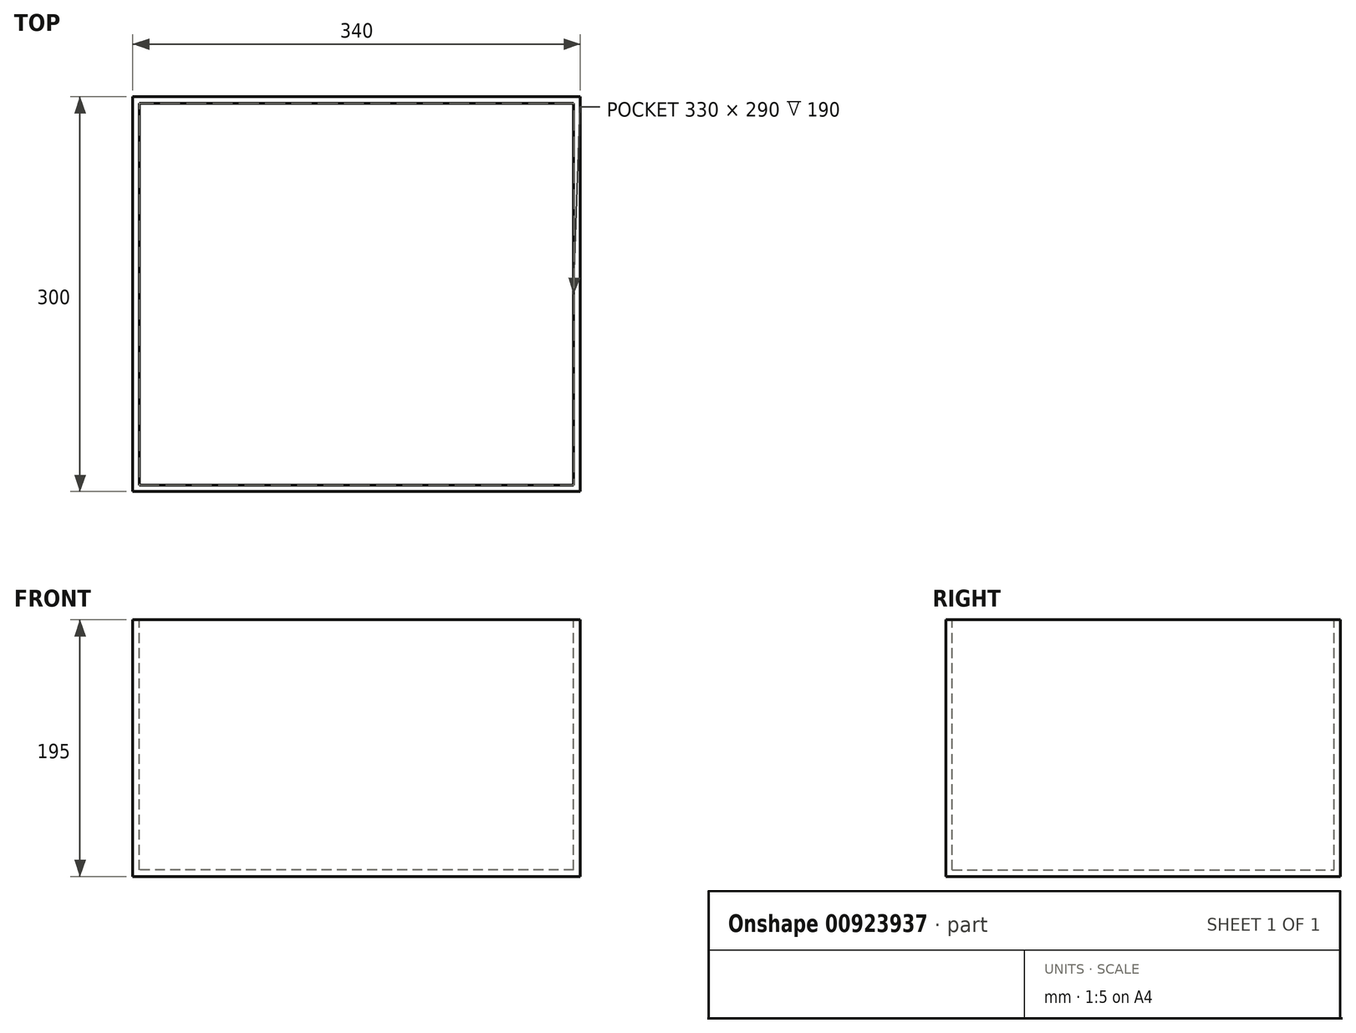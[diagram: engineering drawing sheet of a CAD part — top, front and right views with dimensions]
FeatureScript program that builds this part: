
annotation { "Feature Type Name" : "Feature", "Feature Type Description" : "" }
export const myFeature = defineFeature(function(context is Context, id is Id, definition is map)
    precondition{}
    {
        {
            var Q0;
            Q0=qCreatedBy(makeId("Top.planeOp"),FACE);
            var sketch = newSketch(context, id + "F0", { "sketchPlane" : qUnion([Q0])});
            skLineSegment(sketch, "E0.bottom", {"start": v(168.68, -145) * mm, "end": v(-161.32, -145) * mm});
            skLineSegment(sketch, "E0.top", {"start": v(168.68, 145) * mm, "end": v(-161.32, 145) * mm});
            skLineSegment(sketch, "E0.left", {"start": v(168.68, -145) * mm, "end": v(168.68, 145) * mm});
            skLineSegment(sketch, "E0.right", {"start": v(-161.32, -145) * mm, "end": v(-161.32, 145) * mm});
            skPoint(sketch, "E0.middle", {"position": v(3.68, 0) * mm});
            skLineSegment(sketch, "E1.bottom", {"start": v(173.68, -150) * mm, "end": v(-166.32, -150) * mm});
            skLineSegment(sketch, "E1.top", {"start": v(173.68, 150) * mm, "end": v(-166.32, 150) * mm});
            skLineSegment(sketch, "E1.left", {"start": v(173.68, -150) * mm, "end": v(173.68, 150) * mm});
            skLineSegment(sketch, "E1.right", {"start": v(-166.32, -150) * mm, "end": v(-166.32, 150) * mm});
            skSolve(sketch);
        }
        {
            var Q0;
            Q0 = qSketchRegion(id + "F0", true);
            var Q1;
            Q1=makeQuery(id+"F0.imprint","IMPRINT",FACE,{"disambiguationData":[TD([[makeQuery(id+"F0.imprint","IMPRINT",EDGE,{"derivedFrom":sQuery(id+"F0.wireOp",EDGE,"E0.bottom")}),-1.0]])]});
            extrude(context, id + "F1", {"entities" : qUnion([Q0, Q1]), "depth" : 195 * mm, "offsetDistance" : 25 * mm});
        }
        {
            var Q0;
            Q0=makeQuery(id+"F1.opExtrude","CAP_FACE",FACE,{"disambiguationData":[OSD([sQuery(id+"F0.wireOp",EDGE,"E1.bottom"),sQuery(id+"F0.wireOp",EDGE,"E1.top"),sQuery(id+"F0.wireOp",EDGE,"E1.left"),sQuery(id+"F0.wireOp",EDGE,"E1.right")])],"isStart":false});
            var sketch = newSketch(context, id + "F2", { "sketchPlane" : qUnion([Q0])});
            skLineSegment(sketch, "E2.bottom", {"start": v(168.68, -145) * mm, "end": v(-161.32, -145) * mm});
            skLineSegment(sketch, "E2.top", {"start": v(168.68, 145) * mm, "end": v(-161.32, 145) * mm});
            skLineSegment(sketch, "E2.left", {"start": v(168.68, -145) * mm, "end": v(168.68, 145) * mm});
            skLineSegment(sketch, "E2.right", {"start": v(-161.32, -145) * mm, "end": v(-161.32, 145) * mm});
            skPoint(sketch, "E2.middle", {"position": v(-68.35, 30.33) * mm});
            skLineSegment(sketch, "E3.bottom", {"start": v(173.68, -150) * mm, "end": v(-166.32, -150) * mm});
            skLineSegment(sketch, "E3.top", {"start": v(173.68, 150) * mm, "end": v(-166.32, 150) * mm});
            skLineSegment(sketch, "E3.left", {"start": v(173.68, -150) * mm, "end": v(173.68, 150) * mm});
            skLineSegment(sketch, "E3.right", {"start": v(-166.32, -150) * mm, "end": v(-166.32, 150) * mm});
            skPoint(sketch, "E3.middle", {"position": v(3.68, 0) * mm});
            skSolve(sketch);
        }
        {
            var Q0;
            Q0=makeQuery(id+"F2.imprint","IMPRINT",FACE,{"disambiguationData":[TD([[makeQuery(id+"F2.imprint","IMPRINT",EDGE,{"derivedFrom":sQuery(id+"F2.wireOp",EDGE,"E2.bottom")}),-1.0]])]});
            extrude(context, id + "F3", {"entities" : qUnion([Q0]), "operationType" : NewBodyOperationType.REMOVE, "oppositeDirection" : true, "depth" : 190 * mm, "offsetDistance" : 25 * mm});
        }
    });
